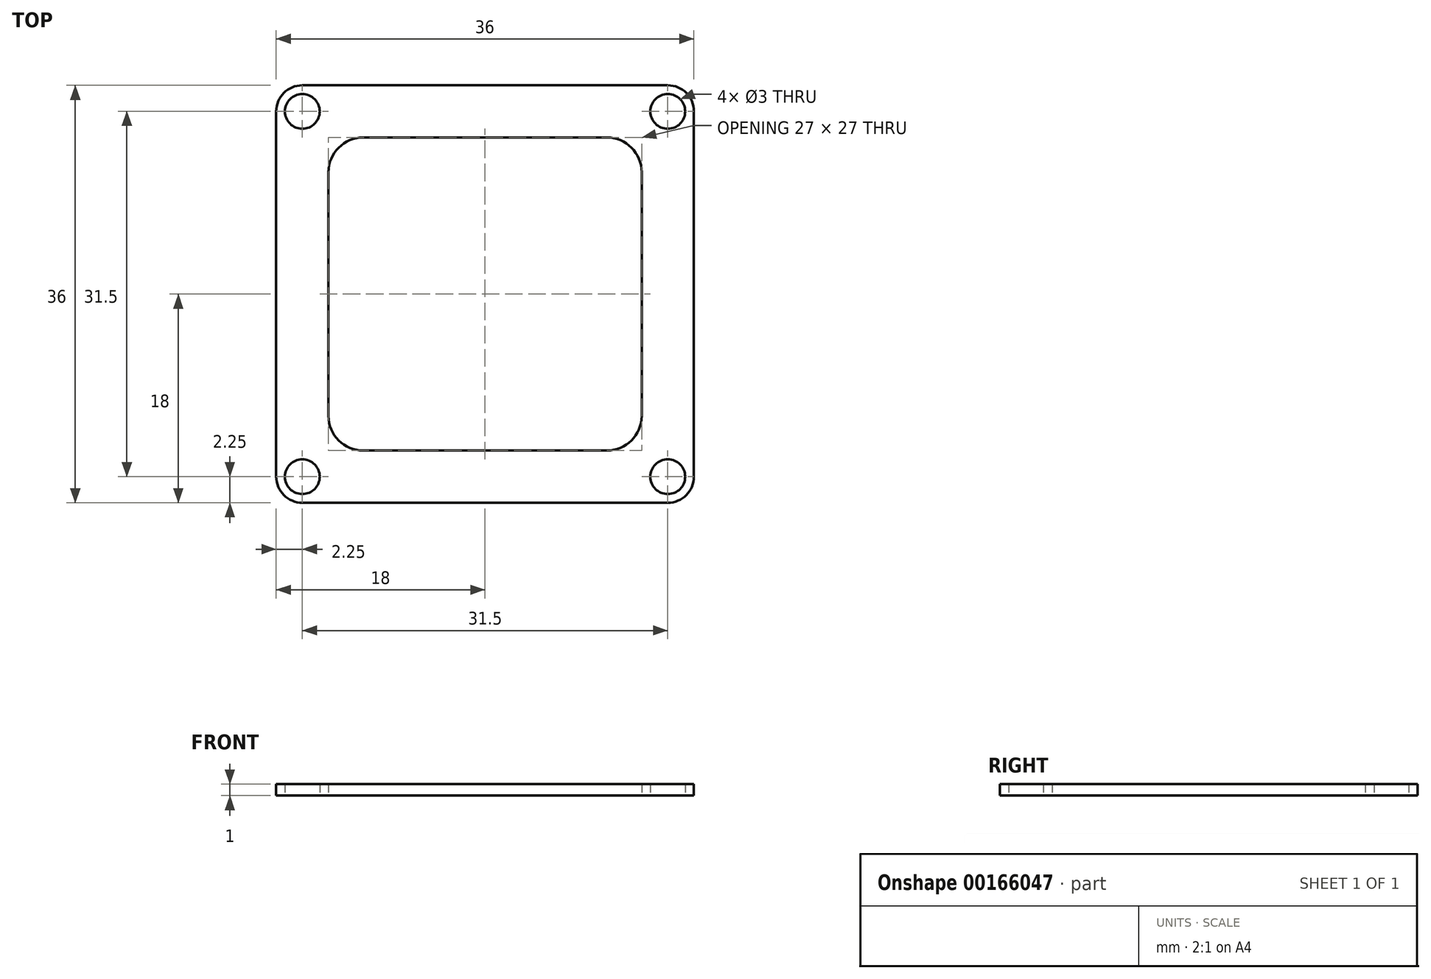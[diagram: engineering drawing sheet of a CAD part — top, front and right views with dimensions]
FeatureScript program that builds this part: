
annotation { "Feature Type Name" : "Feature", "Feature Type Description" : "" }
export const myFeature = defineFeature(function(context is Context, id is Id, definition is map)
    precondition{}
    {
        {
            var Q0;
            Q0=qCreatedBy(makeId("Top.planeOp"),FACE);
            var sketch = newSketch(context, id + "F0", { "sketchPlane" : qUnion([Q0])});
            skLineSegment(sketch, "E0.bottom", {"start": v(18, 18) * mm, "end": v(-18, 18) * mm, "construction": true});
            skLineSegment(sketch, "E0.top", {"start": v(18, -18) * mm, "end": v(-18, -18) * mm, "construction": true});
            skLineSegment(sketch, "E0.left", {"start": v(18, 18) * mm, "end": v(18, -18) * mm, "construction": true});
            skLineSegment(sketch, "E0.right", {"start": v(-18, 18) * mm, "end": v(-18, -18) * mm, "construction": true});
            skPoint(sketch, "E0.middle", {"position": v(0, 0) * mm});
            skLineSegment(sketch, "E1.bottom", {"start": v(15.75, 15.75) * mm, "end": v(-15.75, 15.75) * mm, "construction": true});
            skLineSegment(sketch, "E1.top", {"start": v(15.75, -15.75) * mm, "end": v(-15.75, -15.75) * mm, "construction": true});
            skLineSegment(sketch, "E1.left", {"start": v(15.75, 15.75) * mm, "end": v(15.75, -15.75) * mm, "construction": true});
            skLineSegment(sketch, "E1.right", {"start": v(-15.75, 15.75) * mm, "end": v(-15.75, -15.75) * mm, "construction": true});
            skCircle(sketch, "E2", {"center": v(15.75, 15.75) * mm, "radius": 1.5 * mm});
            skCircle(sketch, "E3", {"center": v(15.75, -15.75) * mm, "radius": 1.5 * mm});
            skCircle(sketch, "E4", {"center": v(-15.75, -15.75) * mm, "radius": 1.5 * mm});
            skCircle(sketch, "E5", {"center": v(-15.75, 15.75) * mm, "radius": 1.5 * mm});
            skLineSegment(sketch, "E6", {"start": v(-47.73, -47.73) * mm, "end": v(0, 0) * mm, "construction": true});
            skLineSegment(sketch, "E7", {"start": v(0, 0) * mm, "end": v(47.73, 47.73) * mm, "construction": true});
            skLineSegment(sketch, "E8", {"start": v(0, 44.74) * mm, "end": v(0, -45.9) * mm, "construction": true});
            skLineSegment(sketch, "E9", {"start": v(-44.2, 0) * mm, "end": v(46.03, 0) * mm, "construction": true});
            skLineSegment(sketch, "E10.MirrorCS", {"start": v(47.73, -47.73) * mm, "end": v(0, 0) * mm, "construction": true});
            skLineSegment(sketch, "E11.MirrorCS", {"start": v(0, 0) * mm, "end": v(-47.73, 47.73) * mm, "construction": true});
            skCircle(sketch, "E12", {"center": v(47.73, 47.73) * mm, "radius": 9 * mm, "construction": true});
            skCircle(sketch, "E13", {"center": v(47.73, 47.73) * mm, "radius": 6 * mm, "construction": true});
            skCircle(sketch, "E14", {"center": v(47.73, 47.73) * mm, "radius": 2.5 * mm, "construction": true});
            skLineSegment(sketch, "E15", {"start": v(47.73, 47.73) * mm, "end": v(47.73, 56.73) * mm, "construction": true});
            skLineSegment(sketch, "E16", {"start": v(47.73, 56.73) * mm, "end": v(47.73, 47.73) * mm, "construction": true});
            skLineSegment(sketch, "E17", {"start": v(47.73, 38.73) * mm, "end": v(47.73, 47.73) * mm, "construction": true});
            skLineSegment(sketch, "E18", {"start": v(47.73, 47.73) * mm, "end": v(56.73, 47.73) * mm, "construction": true});
            skLineSegment(sketch, "E19", {"start": v(38.73, 47.73) * mm, "end": v(47.73, 47.73) * mm, "construction": true});
            skCircle(sketch, "E20", {"center": v(47.73, 53.73) * mm, "radius": 1 * mm, "construction": true});
            skCircle(sketch, "E21", {"center": v(53.73, 47.73) * mm, "radius": 1 * mm, "construction": true});
            skCircle(sketch, "E22", {"center": v(47.73, 41.73) * mm, "radius": 1 * mm, "construction": true});
            skCircle(sketch, "E23", {"center": v(41.73, 47.73) * mm, "radius": 1 * mm, "construction": true});
            skCircle(sketch, "E24.MirrorC", {"center": v(-47.73, 47.73) * mm, "radius": 9 * mm, "construction": true});
            skCircle(sketch, "E25.MirrorC", {"center": v(-47.73, 47.73) * mm, "radius": 6 * mm, "construction": true});
            skCircle(sketch, "E26.MirrorC", {"center": v(-47.73, 41.73) * mm, "radius": 1 * mm, "construction": true});
            skLineSegment(sketch, "E27.MirrorCS", {"start": v(-47.73, 38.73) * mm, "end": v(-47.73, 47.73) * mm, "construction": true});
            skCircle(sketch, "E28.MirrorC", {"center": v(-47.73, 47.73) * mm, "radius": 2.5 * mm, "construction": true});
            skLineSegment(sketch, "E29.MirrorCS", {"start": v(-47.73, 47.73) * mm, "end": v(-56.73, 47.73) * mm, "construction": true});
            skCircle(sketch, "E30.MirrorC", {"center": v(-53.73, 47.73) * mm, "radius": 1 * mm, "construction": true});
            skCircle(sketch, "E31.MirrorC", {"center": v(-47.73, 53.73) * mm, "radius": 1 * mm, "construction": true});
            skLineSegment(sketch, "E32.MirrorCS", {"start": v(-47.73, 56.73) * mm, "end": v(-47.73, 47.73) * mm, "construction": true});
            skCircle(sketch, "E33.MirrorC", {"center": v(-41.73, 47.73) * mm, "radius": 1 * mm, "construction": true});
            skLineSegment(sketch, "E34.MirrorCS", {"start": v(-38.73, 47.73) * mm, "end": v(-47.73, 47.73) * mm, "construction": true});
            skCircle(sketch, "E35.MirrorC", {"center": v(47.73, -47.73) * mm, "radius": 9 * mm, "construction": true});
            skCircle(sketch, "E36.MirrorC", {"center": v(47.73, -47.73) * mm, "radius": 6 * mm, "construction": true});
            skCircle(sketch, "E37.MirrorC", {"center": v(53.73, -47.73) * mm, "radius": 1 * mm, "construction": true});
            skLineSegment(sketch, "E38.MirrorCS", {"start": v(47.73, -47.73) * mm, "end": v(56.73, -47.73) * mm, "construction": true});
            skCircle(sketch, "E39.MirrorC", {"center": v(47.73, -47.73) * mm, "radius": 2.5 * mm, "construction": true});
            skLineSegment(sketch, "E40.MirrorCS", {"start": v(47.73, -38.73) * mm, "end": v(47.73, -47.73) * mm, "construction": true});
            skLineSegment(sketch, "E41.MirrorCS", {"start": v(38.73, -47.73) * mm, "end": v(47.73, -47.73) * mm, "construction": true});
            skCircle(sketch, "E42.MirrorC", {"center": v(41.73, -47.73) * mm, "radius": 1 * mm, "construction": true});
            skCircle(sketch, "E43.MirrorC", {"center": v(47.73, -53.73) * mm, "radius": 1 * mm, "construction": true});
            skLineSegment(sketch, "E44.MirrorCS", {"start": v(47.73, -56.73) * mm, "end": v(47.73, -47.73) * mm, "construction": true});
            skCircle(sketch, "E45.MirrorC", {"center": v(47.73, -41.73) * mm, "radius": 1 * mm, "construction": true});
            skCircle(sketch, "E46.MirrorC", {"center": v(-47.73, -47.73) * mm, "radius": 9 * mm, "construction": true});
            skCircle(sketch, "E47.MirrorC", {"center": v(-41.73, -47.73) * mm, "radius": 1 * mm, "construction": true});
            skLineSegment(sketch, "E48.MirrorCS", {"start": v(-38.73, -47.73) * mm, "end": v(-47.73, -47.73) * mm, "construction": true});
            skCircle(sketch, "E49.MirrorC", {"center": v(-47.73, -47.73) * mm, "radius": 6 * mm, "construction": true});
            skCircle(sketch, "E50.MirrorC", {"center": v(-47.73, -41.73) * mm, "radius": 1 * mm, "construction": true});
            skLineSegment(sketch, "E51.MirrorCS", {"start": v(-47.73, -47.73) * mm, "end": v(-56.73, -47.73) * mm, "construction": true});
            skCircle(sketch, "E52.MirrorC", {"center": v(-53.73, -47.73) * mm, "radius": 1 * mm, "construction": true});
            skCircle(sketch, "E53.MirrorC", {"center": v(-47.73, -53.73) * mm, "radius": 1 * mm, "construction": true});
            skLineSegment(sketch, "E54.MirrorCS", {"start": v(-47.73, -56.73) * mm, "end": v(-47.73, -47.73) * mm, "construction": true});
            skLineSegment(sketch, "E55.MirrorCS", {"start": v(-47.73, -38.73) * mm, "end": v(-47.73, -47.73) * mm, "construction": true});
            skArc(sketch, "E56", {"start": v(-15.75, 18) * mm, "mid": v(-17.34, 17.34) * mm, "end": v(-18, 15.75) * mm});
            skArc(sketch, "E57", {"start": v(18, 15.75) * mm, "mid": v(17.34, 17.34) * mm, "end": v(15.75, 18) * mm});
            skArc(sketch, "E58", {"start": v(15.75, -18) * mm, "mid": v(17.34, -17.34) * mm, "end": v(18, -15.75) * mm});
            skArc(sketch, "E59", {"start": v(-18, -15.75) * mm, "mid": v(-17.34, -17.34) * mm, "end": v(-15.75, -18) * mm});
            skLineSegment(sketch, "E60", {"start": v(-13.5, -10.5) * mm, "end": v(-13.5, 10.5) * mm});
            skLineSegment(sketch, "E61", {"start": v(-10.5, 13.5) * mm, "end": v(10.5, 13.5) * mm});
            skLineSegment(sketch, "E62", {"start": v(13.5, 10.5) * mm, "end": v(13.5, -10.5) * mm});
            skLineSegment(sketch, "E63", {"start": v(10.5, -13.5) * mm, "end": v(-10.5, -13.5) * mm});
            skLineSegment(sketch, "E64", {"start": v(-18, 15.75) * mm, "end": v(-18, -15.75) * mm});
            skLineSegment(sketch, "E65", {"start": v(-15.75, -18) * mm, "end": v(15.75, -18) * mm});
            skLineSegment(sketch, "E66", {"start": v(18, -15.75) * mm, "end": v(18, 15.75) * mm});
            skLineSegment(sketch, "E67", {"start": v(15.75, 18) * mm, "end": v(-15.75, 18) * mm});
            skPoint(sketch, "E68.visualSharp", {"position": v(-13.5, 13.5) * mm});
            skArc(sketch, "E68.filletArc", {"start": v(-10.5, 13.5) * mm, "mid": v(-12.62, 12.62) * mm, "end": v(-13.5, 10.5) * mm});
            skPoint(sketch, "E69.visualSharp", {"position": v(-13.5, -13.5) * mm});
            skArc(sketch, "E69.filletArc", {"start": v(-13.5, -10.5) * mm, "mid": v(-12.62, -12.62) * mm, "end": v(-10.5, -13.5) * mm});
            skPoint(sketch, "E70.visualSharp", {"position": v(13.5, -13.5) * mm});
            skArc(sketch, "E70.filletArc", {"start": v(10.5, -13.5) * mm, "mid": v(12.62, -12.62) * mm, "end": v(13.5, -10.5) * mm});
            skPoint(sketch, "E71.visualSharp", {"position": v(13.5, 13.5) * mm});
            skArc(sketch, "E71.filletArc", {"start": v(13.5, 10.5) * mm, "mid": v(12.62, 12.62) * mm, "end": v(10.5, 13.5) * mm});
            skSolve(sketch);
        }
        {
            var Q0;
            Q0=qCreatedBy(makeId("Top.planeOp"),FACE);
            cPlane(context, id + "F1", {"entities" : qUnion([Q0]), "cplaneType" : CPlaneType.OFFSET, "offset" : 20 * mm, "width" : 150 * mm, "height" : 150 * mm});
        }
        {
            var Q0;
            Q0=qCreatedBy(makeId("Top.planeOp"),FACE);
            cPlane(context, id + "F2", {"entities" : qUnion([Q0]), "cplaneType" : CPlaneType.OFFSET, "offset" : 27 * mm, "width" : 150 * mm, "height" : 150 * mm});
        }
        {
            var Q0;
            Q0=makeQuery(id+"F0.imprint","IMPRINT",FACE,{"disambiguationData":[TD([[makeQuery(id+"F0.imprint","IMPRINT",EDGE,{"derivedFrom":sQuery(id+"F0.wireOp",EDGE,"E2")}),-1.0]])]});
            extrude(context, id + "F3", {"entities" : qUnion([Q0]), "depth" : 1 * mm});
        }
    });
